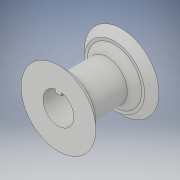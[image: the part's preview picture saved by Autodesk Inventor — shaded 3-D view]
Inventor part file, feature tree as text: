
AUTODESK INVENTOR PART (.ipt)
format: ipt  version: 2017 (Build 210142000, 142)  size: 169,984 bytes
history: native  units: in
note: dims shown in document units (in); Inventor stores cm internally (conversion verified against a paired STEP export)
features: extrude x8, sketch x8, chamfer x1
ambient origin geometry x8: Origin, YZ Plane, XZ Plane, XY Plane, X Axis, Y Axis, Z Axis, Center Point
bodies: Solid1 (feature_tree)
feature tree (17):
  extrude  "Extrusion1"  Depth=1.3in
  extrude  "Extrusion2"  Depth=1.0in
  extrude  "Extrusion3"  Depth=1.0in
  extrude  "Extrusion4"  Depth=0.52in
  extrude  "Extrusion5"  Depth=0.108in
  extrude  "Extrusion6"  Depth=1.1in TaperAngle=0.0deg
  extrude  "Extrusion7"  Depth=0.125in TaperAngle=0.0deg
  chamfer  "Chamfer1"  Distance=1.3in
  extrude  "Extrusion8"  Depth=0.125in TaperAngle=0.0deg
  sketch  "Sketch1"  dims[d0=0.52in d1=1.3in]
  sketch  "Sketch2"  dims[d2=0.25in d3=0.0in d4=1.0in]
  sketch  "Sketch3"  dims[d5=0.6in d6=0.0in d7=1.0in]
  sketch  "Sketch4"  dims[d8=1.3in d9=0.52in]
  sketch  "Sketch5"  dims[d10=0.25in d11=0.0in d12=0.108in]
  sketch  "Sketch6"  dims[d13=0.05in d14=1.1in d15=0.0in]
  sketch  "Sketch7"  dims[d16=1.3in d17=0.125in d18=0.0in]
  sketch  "Sketch8"  dims[d19=1.0in d20=1.3in d21=0.125in d22=0.0in d23=0.7in d24=1.0in d25=0.85in d26=0.0in d27=0.125in d28=0.125in d29=45.0deg d30=0.5375in d31=2.0in d32=0.0in]
